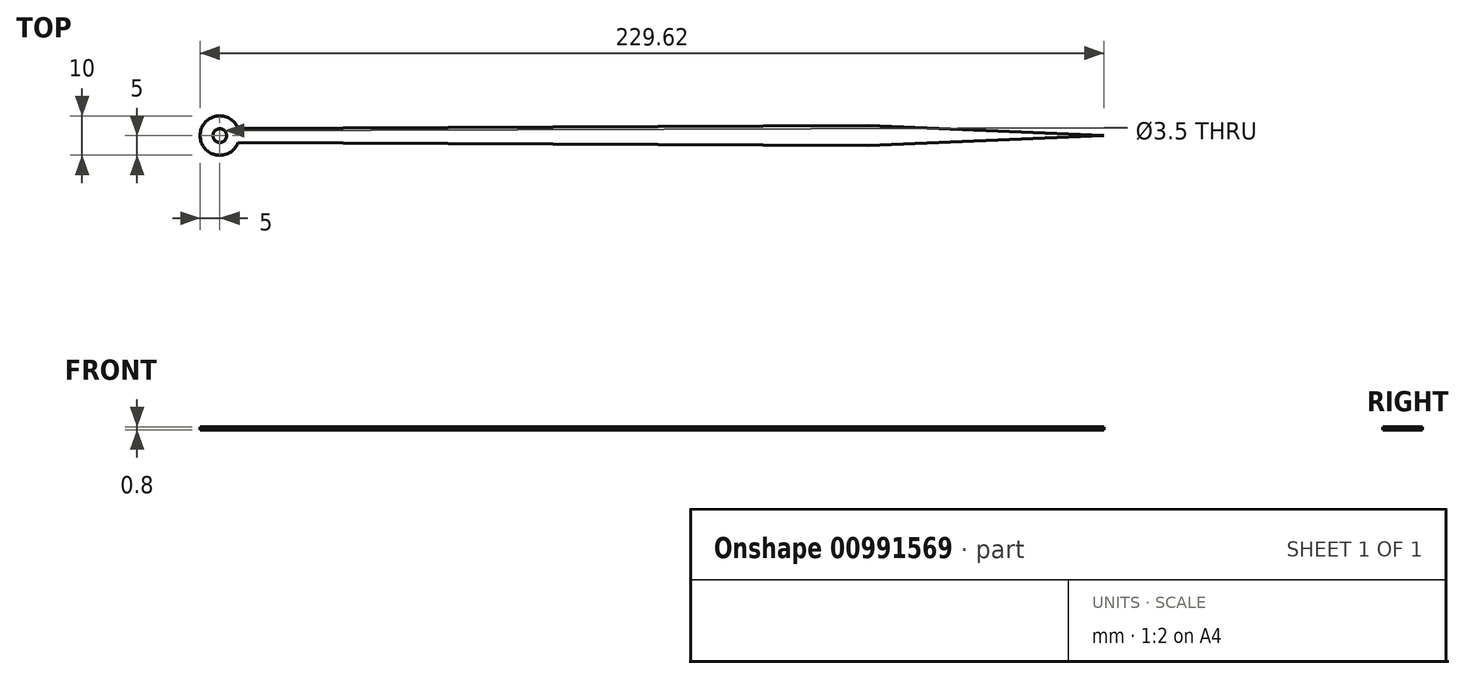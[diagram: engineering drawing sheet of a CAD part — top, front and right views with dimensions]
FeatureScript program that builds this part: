
annotation { "Feature Type Name" : "Feature", "Feature Type Description" : "" }
export const myFeature = defineFeature(function(context is Context, id is Id, definition is map)
    precondition{}
    {
        {
            var Q0;
            Q0=qCreatedBy(makeId("Top.planeOp"),FACE);
            var sketch = newSketch(context, id + "F0", { "sketchPlane" : qUnion([Q0])});
            skCircle(sketch, "E0", {"center": v(0, 0) * mm, "radius": 1.75 * mm});
            skCircle(sketch, "E1", {"center": v(0, 0) * mm, "radius": 5 * mm});
            skLineSegment(sketch, "E2", {"start": v(4.68, 1.77) * mm, "end": v(164.67, 2.5) * mm});
            skLineSegment(sketch, "E3", {"start": v(164.67, 2.5) * mm, "end": v(224.62, 0) * mm});
            skLineSegment(sketch, "E4", {"start": v(224.62, 0) * mm, "end": v(164.67, -2.5) * mm});
            skLineSegment(sketch, "E5", {"start": v(164.67, -2.5) * mm, "end": v(4.68, -1.77) * mm});
            skSolve(sketch);
        }
        {
            var Q0;
            Q0 = qSketchRegion(id + "F0", true);
            extrude(context, id + "F1", {"entities" : qUnion([Q0]), "depth" : .8 * mm, "offsetDistance" : 25 * mm});
        }
    });
